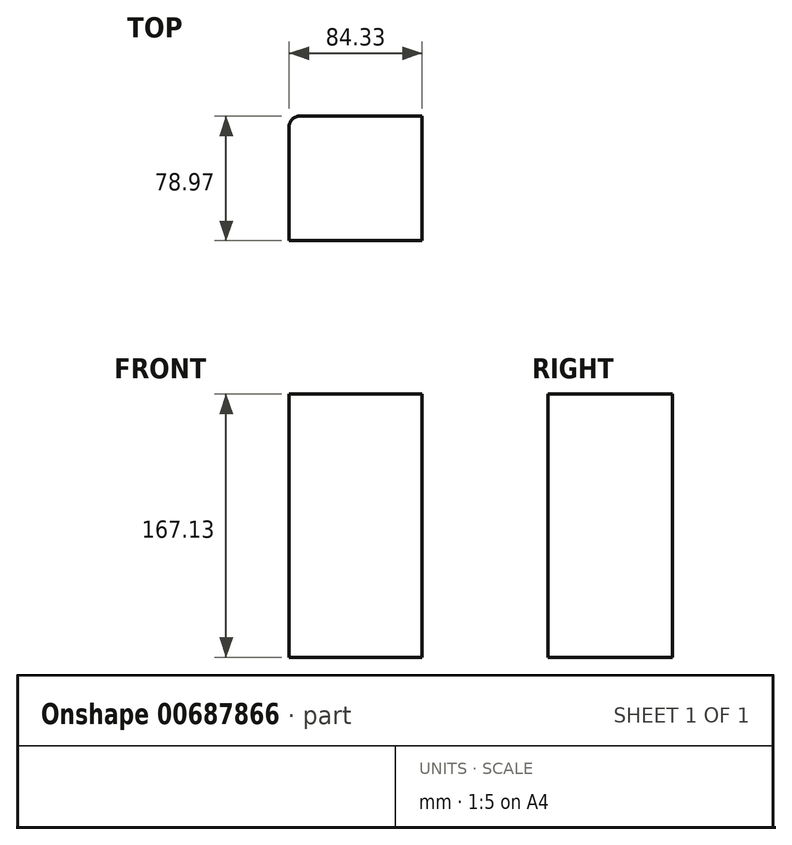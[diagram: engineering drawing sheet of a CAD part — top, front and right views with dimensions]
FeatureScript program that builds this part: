
annotation { "Feature Type Name" : "Feature", "Feature Type Description" : "" }
export const myFeature = defineFeature(function(context is Context, id is Id, definition is map)
    precondition{}
    {
        {
            var Q0;
            Q0=qCreatedBy(makeId("Top.planeOp"),FACE);
            var sketch = newSketch(context, id + "F0", { "sketchPlane" : qUnion([Q0])});
            skLineSegment(sketch, "E0.bottom", {"start": v(6.35, 0) * mm, "end": v(84.33, 0) * mm});
            skLineSegment(sketch, "E0.top", {"start": v(0, -78.97) * mm, "end": v(84.33, -78.97) * mm});
            skLineSegment(sketch, "E0.left", {"start": v(0, -6.35) * mm, "end": v(0, -78.97) * mm});
            skLineSegment(sketch, "E0.right", {"start": v(84.33, 0) * mm, "end": v(84.33, -78.97) * mm});
            skPoint(sketch, "E1.visualSharp", {"position": v(0, 0) * mm});
            skArc(sketch, "E1.filletArc", {"start": v(6.35, 0) * mm, "mid": v(1.86, -1.86) * mm, "end": v(0, -6.35) * mm});
            skSolve(sketch);
        }
        {
            var Q0;
            Q0 = qSketchRegion(id + "F0", true);
            extrude(context, id + "F1", {"entities" : qUnion([Q0]), "depth" : 50.8 * mm, "offsetDistance" : 25.4 * mm});
        }
        {
            var Q0;
            Q0=makeQuery(id+"F1.opExtrude","CAP_FACE",FACE,{"disambiguationData":[OSD([sQuery(id+"F0.wireOp",EDGE,"E0.bottom"),sQuery(id+"F0.wireOp",EDGE,"E0.top"),sQuery(id+"F0.wireOp",EDGE,"E0.left"),sQuery(id+"F0.wireOp",EDGE,"E0.right"),sQuery(id+"F0.wireOp",EDGE,"E1.filletArc")])],"isStart":false});
            extrude(context, id + "F2", {"entities" : qUnion([Q0]), "operationType" : NewBodyOperationType.ADD, "depth" : 116.33 * mm, "offsetDistance" : 25.4 * mm});
        }
    });
